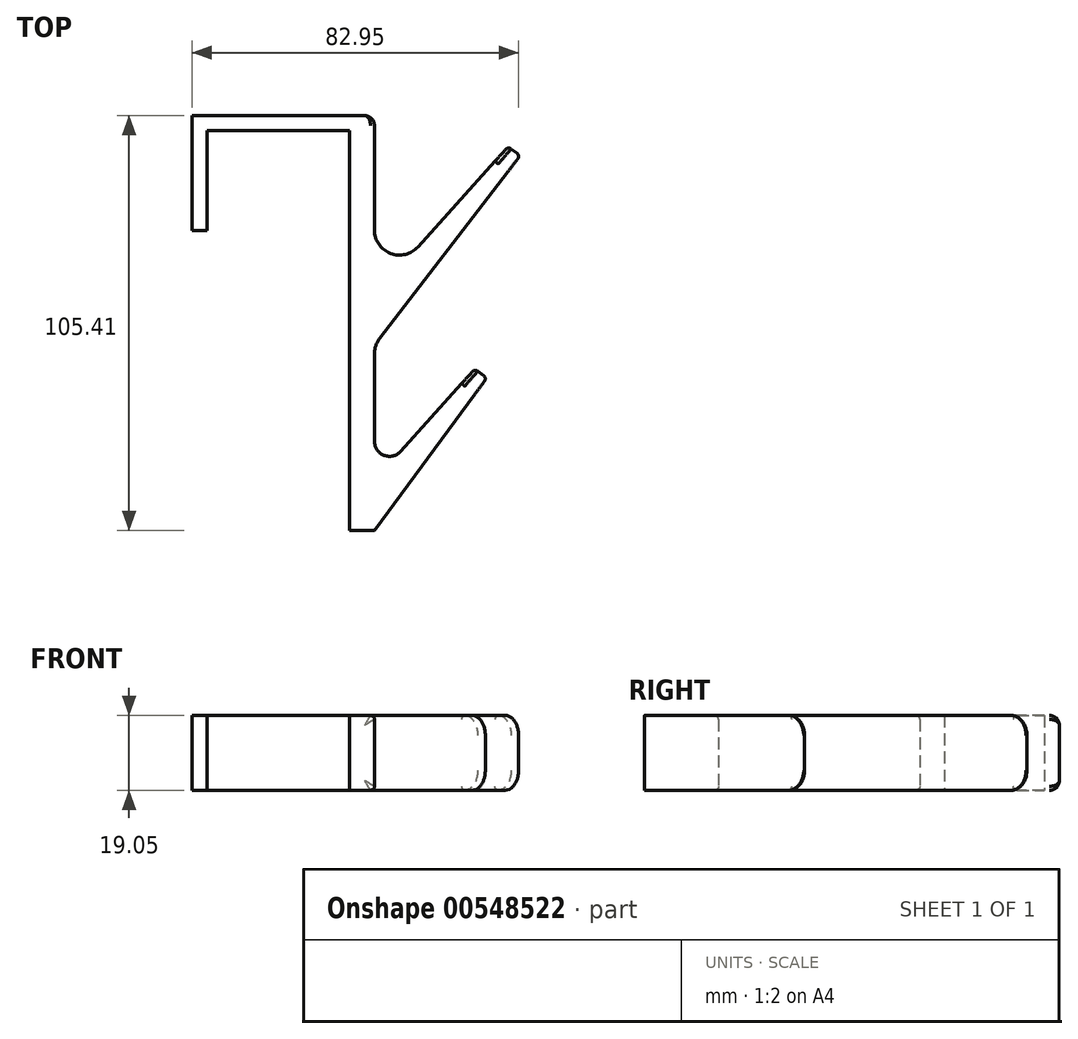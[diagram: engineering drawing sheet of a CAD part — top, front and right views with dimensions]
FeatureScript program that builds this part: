
annotation { "Feature Type Name" : "Feature", "Feature Type Description" : "" }
export const myFeature = defineFeature(function(context is Context, id is Id, definition is map)
    precondition{}
    {
        {
            var Q0;
            Q0=qCreatedBy(makeId("Top.planeOp"),FACE);
            var sketch = newSketch(context, id + "F0", { "sketchPlane" : qUnion([Q0])});
            skLineSegment(sketch, "E0", {"start": v(-36.2, 0) * mm, "end": v(-36.2, 25.4) * mm});
            skLineSegment(sketch, "E1", {"start": v(-36.2, 25.4) * mm, "end": v(0, 25.4) * mm});
            skLineSegment(sketch, "E2", {"start": v(0, 25.4) * mm, "end": v(0, -76.2) * mm});
            skLineSegment(sketch, "E3", {"start": v(0, -76.2) * mm, "end": v(6.35, -76.2) * mm});
            skLineSegment(sketch, "E4", {"start": v(6.35, -76.2) * mm, "end": v(34.91, -37.45) * mm});
            skLineSegment(sketch, "E5", {"start": v(34.91, -37.45) * mm, "end": v(31.84, -35.19) * mm});
            skLineSegment(sketch, "E6", {"start": v(31.84, -35.19) * mm, "end": v(13, -56.12) * mm});
            skLineSegment(sketch, "E7", {"start": v(6.35, -53.57) * mm, "end": v(6.35, -31.3) * mm});
            skLineSegment(sketch, "E8", {"start": v(7.67, -27.43) * mm, "end": v(43.36, 19) * mm});
            skLineSegment(sketch, "E9", {"start": v(43.36, 19) * mm, "end": v(40.34, 21.31) * mm});
            skLineSegment(sketch, "E10", {"start": v(40.34, 21.31) * mm, "end": v(17.42, -4.15) * mm});
            skLineSegment(sketch, "E11", {"start": v(6.35, 0.1) * mm, "end": v(6.35, 29.21) * mm});
            skLineSegment(sketch, "E12", {"start": v(6.35, 29.21) * mm, "end": v(-40, 29.21) * mm});
            skLineSegment(sketch, "E13", {"start": v(-40, 29.21) * mm, "end": v(-40, 0) * mm});
            skLineSegment(sketch, "E14", {"start": v(-40, 0) * mm, "end": v(-36.2, 0) * mm});
            skPoint(sketch, "E15.visualSharp", {"position": v(6.35, -16.44) * mm});
            skArc(sketch, "E15.filletArc", {"start": v(6.35, 0.1) * mm, "mid": v(10.42, -5.82) * mm, "end": v(17.42, -4.15) * mm});
            skPoint(sketch, "E16.visualSharp", {"position": v(6.35, -63.5) * mm});
            skPoint(sketch, "E17.visualSharp", {"position": v(6.35, -29.14) * mm});
            skArc(sketch, "E17.filletArc", {"start": v(7.67, -27.43) * mm, "mid": v(6.69, -29.25) * mm, "end": v(6.35, -31.3) * mm});
            skArc(sketch, "E18.filletArc", {"start": v(6.35, -53.57) * mm, "mid": v(8.8, -57.13) * mm, "end": v(13, -56.12) * mm});
            skSolve(sketch);
        }
        {
            var Q0;
            Q0 = qSketchRegion(id + "F0", true);
            extrude(context, id + "F1", {"entities" : qUnion([Q0]), "depth" : 19.05 * mm, "offsetDistance" : 25.4 * mm});
        }
        {
            var Q0;
            Q0=makeQuery(id+"F1.opExtrude","CAP_EDGE",EDGE,{"disambiguationData":[OSD([sQuery(id+"F0.wireOp",EDGE,"E9")])],"isStart":false});
            var Q1;
            Q1=makeQuery(id+"F1.opExtrude","CAP_EDGE",EDGE,{"disambiguationData":[OSD([sQuery(id+"F0.wireOp",EDGE,"E9")])],"isStart":true});
            var Q2;
            Q2=makeQuery(id+"F1.opExtrude","CAP_EDGE",EDGE,{"disambiguationData":[OSD([sQuery(id+"F0.wireOp",EDGE,"E5")])],"isStart":true});
            var Q3;
            Q3=makeQuery(id+"F1.opExtrude","CAP_EDGE",EDGE,{"disambiguationData":[OSD([sQuery(id+"F0.wireOp",EDGE,"E5")])],"isStart":false});
            fillet(context, id + "F2", {"entities" : qUnion([Q0, Q1, Q2, Q3]), "radius" : 5.08 * mm, "tangentPropagation" : true, "allowEdgeOverflow" : false});
        }
        {
            var Q0;
            Q0=makeQuery(id+"F1.opExtrude","SWEPT_EDGE",EDGE,{"disambiguationData":[OSD([sQuery(id+"F0.wireOp",EDGE,"E9"),sQuery(id+"F0.wireOp",EDGE,"E10")])]});
            var Q1;
            Q1=makeQuery(id+"F1.opExtrude","SWEPT_EDGE",EDGE,{"disambiguationData":[OSD([sQuery(id+"F0.wireOp",EDGE,"E8"),sQuery(id+"F0.wireOp",EDGE,"E9")])]});
            var Q2;
            Q2=makeQuery(id+"F1.opExtrude","SWEPT_EDGE",EDGE,{"disambiguationData":[OSD([sQuery(id+"F0.wireOp",EDGE,"E4"),sQuery(id+"F0.wireOp",EDGE,"E5")])]});
            fillet(context, id + "F3", {"entities" : qUnion([Q0, Q1, Q2]), "radius" : 1.02 * mm, "tangentPropagation" : true, "allowEdgeOverflow" : false});
        }
        {
            var Q0;
            Q0=makeQuery(id+"F1.opExtrude","SWEPT_EDGE",EDGE,{"disambiguationData":[OSD([sQuery(id+"F0.wireOp",EDGE,"E11"),sQuery(id+"F0.wireOp",EDGE,"E12")])]});
            fillet(context, id + "F4", {"entities" : qUnion([Q0]), "radius" : 2.54 * mm, "tangentPropagation" : true, "allowEdgeOverflow" : false});
        }
    });
